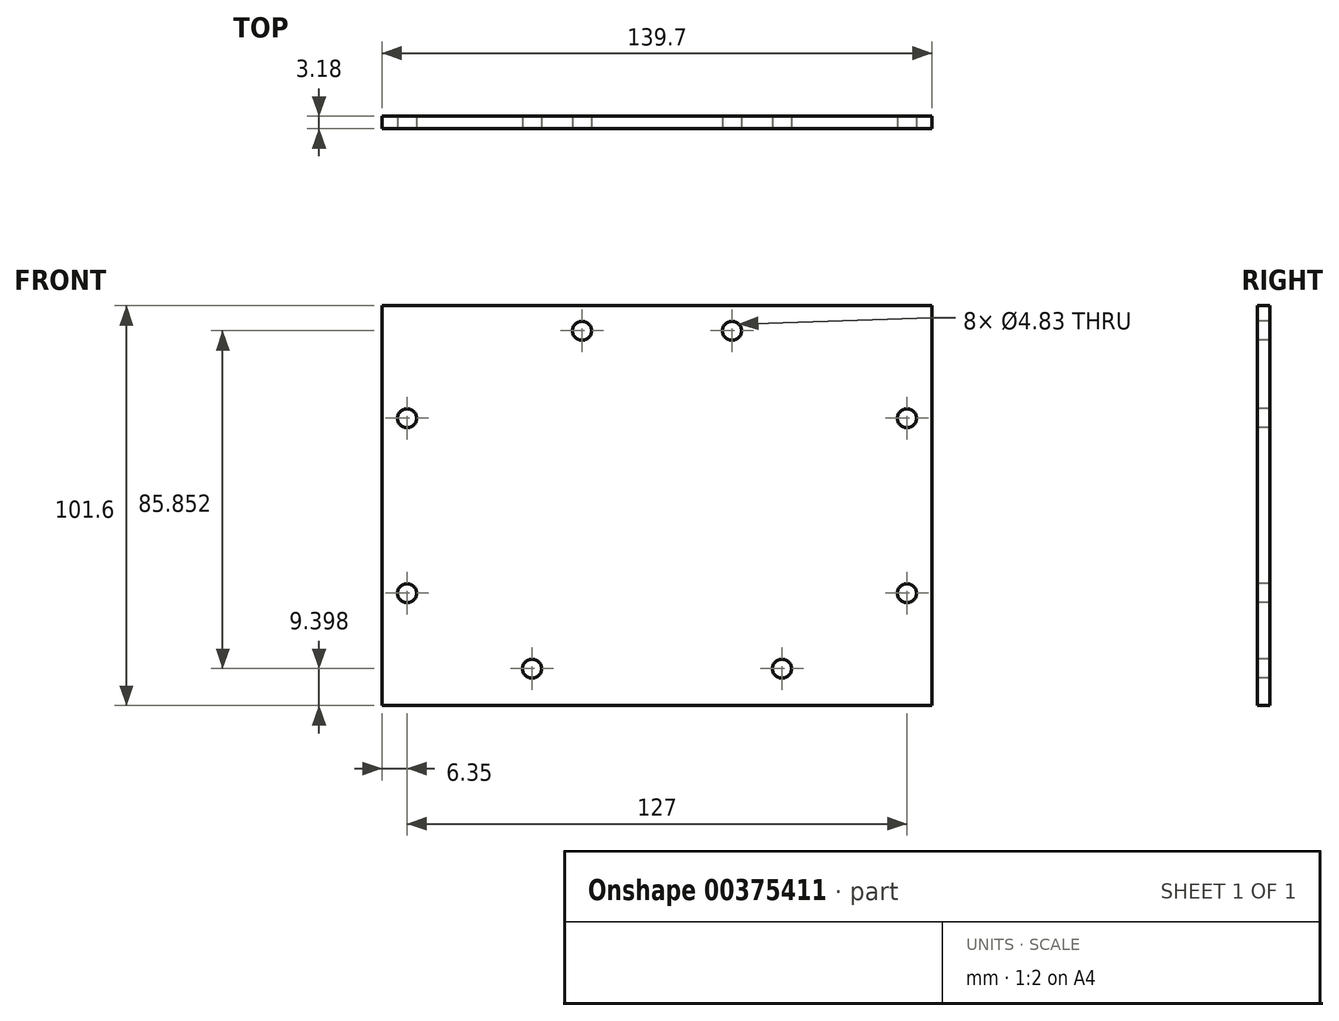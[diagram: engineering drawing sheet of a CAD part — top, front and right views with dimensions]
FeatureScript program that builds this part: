
annotation { "Feature Type Name" : "Feature", "Feature Type Description" : "" }
export const myFeature = defineFeature(function(context is Context, id is Id, definition is map)
    precondition{}
    {
        {
            var Q0;
            Q0=qCreatedBy(makeId("Front.planeOp"),FACE);
            var sketch = newSketch(context, id + "F0", { "sketchPlane" : qUnion([Q0])});
            skLineSegment(sketch, "E0.bottom", {"start": v(-69.85, 50.8) * mm, "end": v(69.85, 50.8) * mm});
            skLineSegment(sketch, "E0.top", {"start": v(-69.85, -50.8) * mm, "end": v(69.85, -50.8) * mm});
            skLineSegment(sketch, "E0.left", {"start": v(-69.85, 50.8) * mm, "end": v(-69.85, -50.8) * mm});
            skLineSegment(sketch, "E0.right", {"start": v(69.85, 50.8) * mm, "end": v(69.85, -50.8) * mm});
            skPoint(sketch, "E0.middle", {"position": v(0, 0) * mm});
            skSolve(sketch);
        }
        {
            var Q0;
            Q0=qSketchRegion(id+"F0",true);
            extrude(context, id + "F1", {"entities" : qUnion([Q0]), "depth" : 3.17 * mm});
        }
        {
            var Q0;
            Q0=makeQuery(id+"F1.opExtrude","CAP_FACE",FACE,{"disambiguationData":[OSD([sQuery(id+"F0.wireOp",EDGE,"E0.bottom"),sQuery(id+"F0.wireOp",EDGE,"E0.top"),sQuery(id+"F0.wireOp",EDGE,"E0.left"),sQuery(id+"F0.wireOp",EDGE,"E0.right")])],"isStart":false});
            var sketch = newSketch(context, id + "F2", { "sketchPlane" : qUnion([Q0])});
            skCircle(sketch, "E1", {"center": v(-19.05, 44.45) * mm, "radius": 2.41 * mm});
            skSolve(sketch);
        }
        {
            var Q0;
            Q0=qSketchRegion(id+"F2",true);
            extrude(context, id + "F3", {"entities" : qUnion([Q0]), "operationType" : NewBodyOperationType.REMOVE, "endBound" : BoundingType.THROUGH_ALL, "oppositeDirection" : true, "depth" : 25.4 * mm});
        }
        {
            var Q0;
            Q0=makeQuery(id+"F1.opExtrude","CAP_FACE",FACE,{"disambiguationData":[OSD([sQuery(id+"F0.wireOp",EDGE,"E0.bottom"),sQuery(id+"F0.wireOp",EDGE,"E0.top"),sQuery(id+"F0.wireOp",EDGE,"E0.left"),sQuery(id+"F0.wireOp",EDGE,"E0.right")])],"isStart":false});
            var sketch = newSketch(context, id + "F4", { "sketchPlane" : qUnion([Q0])});
            skCircle(sketch, "E2", {"center": v(19.05, 44.45) * mm, "radius": 2.41 * mm});
            skSolve(sketch);
        }
        {
            var Q0;
            Q0=qSketchRegion(id+"F4",true);
            extrude(context, id + "F5", {"entities" : qUnion([Q0]), "operationType" : NewBodyOperationType.REMOVE, "endBound" : BoundingType.THROUGH_ALL, "oppositeDirection" : true, "depth" : 25.4 * mm});
        }
        {
            var Q0;
            Q0=makeQuery(id+"F1.opExtrude","CAP_FACE",FACE,{"disambiguationData":[OSD([sQuery(id+"F0.wireOp",EDGE,"E0.bottom"),sQuery(id+"F0.wireOp",EDGE,"E0.top"),sQuery(id+"F0.wireOp",EDGE,"E0.left"),sQuery(id+"F0.wireOp",EDGE,"E0.right")])],"isStart":false});
            var sketch = newSketch(context, id + "F6", { "sketchPlane" : qUnion([Q0])});
            skCircle(sketch, "E3", {"center": v(-31.75, -41.4) * mm, "radius": 2.41 * mm});
            skSolve(sketch);
        }
        {
            var Q0;
            Q0=qSketchRegion(id+"F6",true);
            extrude(context, id + "F7", {"entities" : qUnion([Q0]), "operationType" : NewBodyOperationType.REMOVE, "endBound" : BoundingType.THROUGH_ALL, "oppositeDirection" : true, "depth" : 25.4 * mm});
        }
        {
            var Q0;
            Q0=makeQuery(id+"F1.opExtrude","CAP_FACE",FACE,{"disambiguationData":[OSD([sQuery(id+"F0.wireOp",EDGE,"E0.bottom"),sQuery(id+"F0.wireOp",EDGE,"E0.top"),sQuery(id+"F0.wireOp",EDGE,"E0.left"),sQuery(id+"F0.wireOp",EDGE,"E0.right")])],"isStart":false});
            var sketch = newSketch(context, id + "F8", { "sketchPlane" : qUnion([Q0])});
            skCircle(sketch, "E4", {"center": v(31.75, -41.4) * mm, "radius": 2.41 * mm});
            skCircle(sketch, "E5.0", {"center": v(-31.75, -41.4) * mm, "radius": 2.41 * mm});
            skSolve(sketch);
        }
        {
            var Q0;
            Q0=qSketchRegion(id+"F8",true);
            extrude(context, id + "F9", {"entities" : qUnion([Q0]), "operationType" : NewBodyOperationType.REMOVE, "endBound" : BoundingType.THROUGH_ALL, "oppositeDirection" : true, "depth" : 25.4 * mm});
        }
        {
            var Q0;
            Q0=makeQuery(id+"F1.opExtrude","CAP_FACE",FACE,{"disambiguationData":[OSD([sQuery(id+"F0.wireOp",EDGE,"E0.bottom"),sQuery(id+"F0.wireOp",EDGE,"E0.top"),sQuery(id+"F0.wireOp",EDGE,"E0.left"),sQuery(id+"F0.wireOp",EDGE,"E0.right")])],"isStart":false});
            var sketch = newSketch(context, id + "F10", { "sketchPlane" : qUnion([Q0])});
            skCircle(sketch, "E6", {"center": v(-63.5, 22.23) * mm, "radius": 2.41 * mm});
            skSolve(sketch);
        }
        {
            var Q0;
            Q0=qSketchRegion(id+"F10",true);
            extrude(context, id + "F11", {"entities" : qUnion([Q0]), "operationType" : NewBodyOperationType.REMOVE, "endBound" : BoundingType.THROUGH_ALL, "oppositeDirection" : true, "depth" : 25.4 * mm});
        }
        {
            var Q0;
            Q0=makeQuery(id+"F1.opExtrude","CAP_FACE",FACE,{"disambiguationData":[OSD([sQuery(id+"F0.wireOp",EDGE,"E0.bottom"),sQuery(id+"F0.wireOp",EDGE,"E0.top"),sQuery(id+"F0.wireOp",EDGE,"E0.left"),sQuery(id+"F0.wireOp",EDGE,"E0.right")])],"isStart":false});
            var sketch = newSketch(context, id + "F12", { "sketchPlane" : qUnion([Q0])});
            skCircle(sketch, "E7", {"center": v(-63.5, -22.23) * mm, "radius": 2.41 * mm});
            skSolve(sketch);
        }
        {
            var Q0;
            Q0=qSketchRegion(id+"F12",true);
            extrude(context, id + "F13", {"entities" : qUnion([Q0]), "operationType" : NewBodyOperationType.REMOVE, "endBound" : BoundingType.THROUGH_ALL, "oppositeDirection" : true, "depth" : 25.4 * mm});
        }
        {
            var Q0;
            Q0=makeQuery(id+"F1.opExtrude","CAP_FACE",FACE,{"disambiguationData":[OSD([sQuery(id+"F0.wireOp",EDGE,"E0.bottom"),sQuery(id+"F0.wireOp",EDGE,"E0.top"),sQuery(id+"F0.wireOp",EDGE,"E0.left"),sQuery(id+"F0.wireOp",EDGE,"E0.right")])],"isStart":false});
            var sketch = newSketch(context, id + "F14", { "sketchPlane" : qUnion([Q0])});
            skCircle(sketch, "E8", {"center": v(63.5, 22.23) * mm, "radius": 2.41 * mm});
            skSolve(sketch);
        }
        {
            var Q0;
            Q0=qSketchRegion(id+"F14",true);
            extrude(context, id + "F15", {"entities" : qUnion([Q0]), "operationType" : NewBodyOperationType.REMOVE, "endBound" : BoundingType.THROUGH_ALL, "oppositeDirection" : true, "depth" : 25.4 * mm});
        }
        {
            var Q0;
            Q0=makeQuery(id+"F1.opExtrude","CAP_FACE",FACE,{"disambiguationData":[OSD([sQuery(id+"F0.wireOp",EDGE,"E0.bottom"),sQuery(id+"F0.wireOp",EDGE,"E0.top"),sQuery(id+"F0.wireOp",EDGE,"E0.left"),sQuery(id+"F0.wireOp",EDGE,"E0.right")])],"isStart":false});
            var sketch = newSketch(context, id + "F16", { "sketchPlane" : qUnion([Q0])});
            skCircle(sketch, "E9", {"center": v(63.5, -22.23) * mm, "radius": 2.41 * mm});
            skCircle(sketch, "E10.0", {"center": v(63.5, 22.23) * mm, "radius": 2.41 * mm});
            skSolve(sketch);
        }
        {
            var Q0;
            Q0=qSketchRegion(id+"F16",true);
            extrude(context, id + "F17", {"entities" : qUnion([Q0]), "operationType" : NewBodyOperationType.REMOVE, "endBound" : BoundingType.THROUGH_ALL, "oppositeDirection" : true, "depth" : 25.4 * mm});
        }
    });
